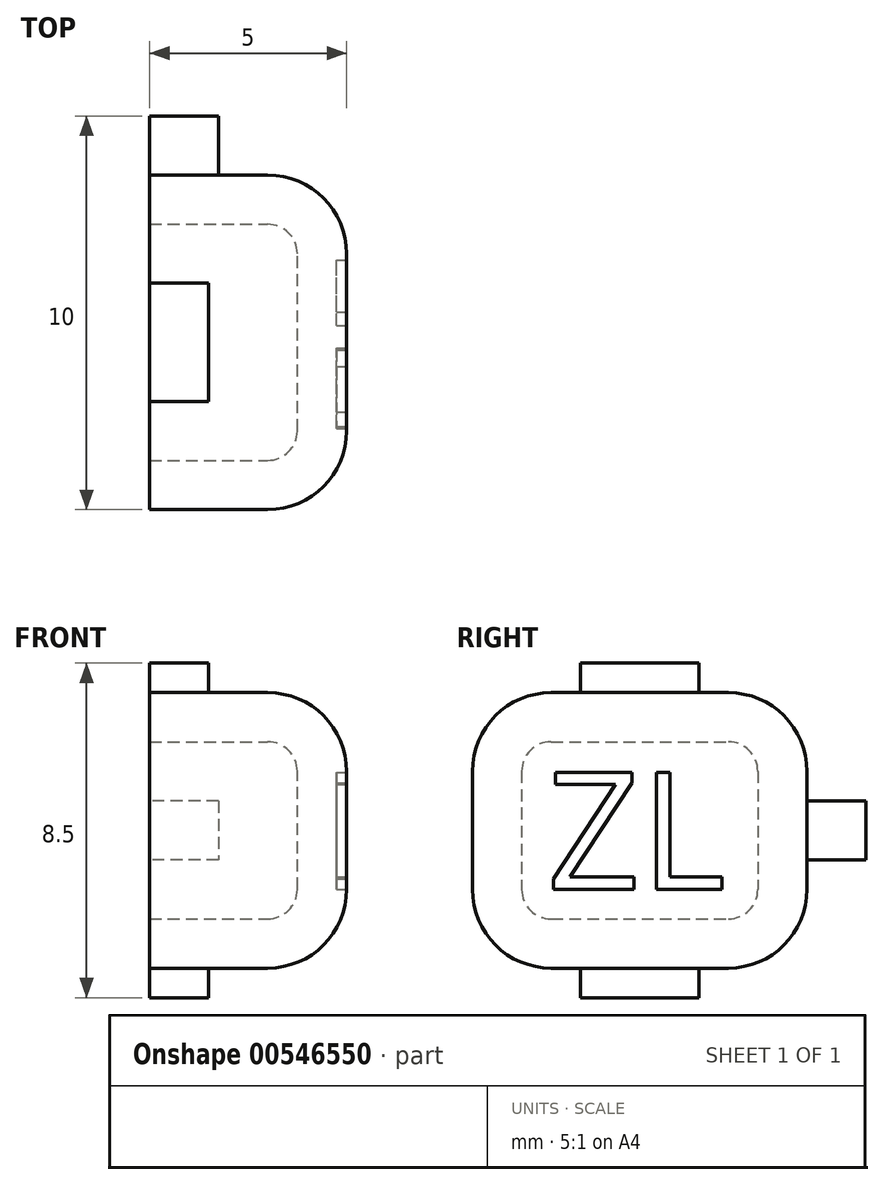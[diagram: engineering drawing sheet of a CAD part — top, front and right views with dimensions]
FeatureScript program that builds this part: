
annotation { "Feature Type Name" : "Feature", "Feature Type Description" : "" }
export const myFeature = defineFeature(function(context is Context, id is Id, definition is map)
    precondition{}
    {
        {
            var Q0;
            Q0=qCreatedBy(makeId("Right.planeOp"),FACE);
            var sketch = newSketch(context, id + "F0", { "sketchPlane" : qUnion([Q0])});
            skLineSegment(sketch, "E0.bottom", {"start": v(-4.25, 3.5) * mm, "end": v(4.25, 3.5) * mm});
            skLineSegment(sketch, "E0.top", {"start": v(-4.25, -3.5) * mm, "end": v(4.25, -3.5) * mm});
            skLineSegment(sketch, "E0.left", {"start": v(-4.25, 3.5) * mm, "end": v(-4.25, -3.5) * mm});
            skLineSegment(sketch, "E0.right", {"start": v(4.25, 3.5) * mm, "end": v(4.25, -3.5) * mm});
            skPoint(sketch, "E0.middle", {"position": v(0, 0) * mm});
            skSolve(sketch);
        }
        {
            var Q0;
            Q0=makeQuery(id+"F0.imprint","IMPRINT",FACE,{"disambiguationData":[TD([[makeQuery(id+"F0.imprint","IMPRINT",EDGE,{"derivedFrom":sQuery(id+"F0.wireOp",EDGE,"E0.bottom")}),-1.0]])]});
            extrude(context, id + "F1", {"entities" : qUnion([Q0]), "endBound" : BoundingType.SYMMETRIC, "depth" : 5 * mm, "offsetDistance" : 25 * mm});
        }
        {
            var Q0;
            Q0=makeQuery(id+"F1.opExtrude","CAP_FACE",FACE,{"disambiguationData":[OSD([sQuery(id+"F0.wireOp",EDGE,"E0.bottom"),sQuery(id+"F0.wireOp",EDGE,"E0.top"),sQuery(id+"F0.wireOp",EDGE,"E0.left"),sQuery(id+"F0.wireOp",EDGE,"E0.right")])],"isStart":false});
            var Q1;
            Q1=makeQuery(id+"F1.opExtrude","SWEPT_EDGE",EDGE,{"disambiguationData":[OSD([sQuery(id+"F0.wireOp",EDGE,"E0.bottom"),sQuery(id+"F0.wireOp",EDGE,"E0.left")])]});
            var Q2;
            Q2=makeQuery(id+"F1.opExtrude","SWEPT_EDGE",EDGE,{"disambiguationData":[OSD([sQuery(id+"F0.wireOp",EDGE,"E0.bottom"),sQuery(id+"F0.wireOp",EDGE,"E0.right")])]});
            var Q3;
            Q3=makeQuery(id+"F1.opExtrude","SWEPT_EDGE",EDGE,{"disambiguationData":[OSD([sQuery(id+"F0.wireOp",EDGE,"E0.top"),sQuery(id+"F0.wireOp",EDGE,"E0.right")])]});
            var Q4;
            Q4=makeQuery(id+"F1.opExtrude","SWEPT_EDGE",EDGE,{"disambiguationData":[OSD([sQuery(id+"F0.wireOp",EDGE,"E0.top"),sQuery(id+"F0.wireOp",EDGE,"E0.left")])]});
            fillet(context, id + "F2", {"entities" : qUnion([Q0, Q1, Q2, Q3, Q4]), "radius" : 2 * mm, "tangentPropagation" : true, "allowEdgeOverflow" : false});
        }
        {
            var Q0;
            Q0=makeQuery(id+"F1.opExtrude","CAP_FACE",FACE,{"disambiguationData":[OSD([sQuery(id+"F0.wireOp",EDGE,"E0.bottom"),sQuery(id+"F0.wireOp",EDGE,"E0.top"),sQuery(id+"F0.wireOp",EDGE,"E0.left"),sQuery(id+"F0.wireOp",EDGE,"E0.right")])],"isStart":true});
            shell(context, id + "F3", {"entities" : qUnion([Q0]), "thickness" : 1.25 * mm});
        }
        {
            var Q0;
            Q0=makeQuery(id+"F1.opExtrude","CAP_FACE",FACE,{"disambiguationData":[OSD([sQuery(id+"F0.wireOp",EDGE,"E0.bottom"),sQuery(id+"F0.wireOp",EDGE,"E0.top"),sQuery(id+"F0.wireOp",EDGE,"E0.left"),sQuery(id+"F0.wireOp",EDGE,"E0.right")])],"isStart":false});
            var sketch = newSketch(context, id + "F4", { "sketchPlane" : qUnion([Q0])});
            skText(sketch, "E1", { "text": "ZL", "fontName": "OpenSans-Regular.ttf"});
            const initialGuessF4  = {"E1": [-0.00236, -0.0015, 1, 0, 0.003]};
            skSetInitialGuess(sketch, initialGuessF4);
            skSolve(sketch);
        }
        {
            var Q0;
            Q0=qSketchRegion(id+"F4",true);
            extrude(context, id + "F5", {"entities" : qUnion([Q0]), "operationType" : NewBodyOperationType.REMOVE, "oppositeDirection" : true, "depth" : .25 * mm, "offsetDistance" : 25 * mm});
        }
        {
            var Q0;
            Q0=makeQuery(id+"F1.opExtrude","CAP_FACE",FACE,{"disambiguationData":[OSD([sQuery(id+"F0.wireOp",EDGE,"E0.bottom"),sQuery(id+"F0.wireOp",EDGE,"E0.top"),sQuery(id+"F0.wireOp",EDGE,"E0.left"),sQuery(id+"F0.wireOp",EDGE,"E0.right")])],"isStart":true});
            var sketch = newSketch(context, id + "F6", { "sketchPlane" : qUnion([Q0])});
            skLineSegment(sketch, "E2.bottom", {"start": v(1.5, 3.5) * mm, "end": v(-1.5, 3.5) * mm});
            skLineSegment(sketch, "E2.top", {"start": v(1.5, 4.25) * mm, "end": v(-1.5, 4.25) * mm});
            skLineSegment(sketch, "E2.left", {"start": v(1.5, 3.5) * mm, "end": v(1.5, 4.25) * mm});
            skLineSegment(sketch, "E2.right", {"start": v(-1.5, 3.5) * mm, "end": v(-1.5, 4.25) * mm});
            skPoint(sketch, "E2.middle", {"position": v(0, 3.87) * mm});
            skLineSegment(sketch, "E3.MirrorCS", {"start": v(1.5, -3.5) * mm, "end": v(1.5, -4.25) * mm});
            skLineSegment(sketch, "E4.MirrorCS", {"start": v(-1.5, -3.5) * mm, "end": v(-1.5, -4.25) * mm});
            skLineSegment(sketch, "E5.MirrorCS", {"start": v(1.5, -4.25) * mm, "end": v(-1.5, -4.25) * mm});
            skLineSegment(sketch, "E6.MirrorCS", {"start": v(1.5, -3.5) * mm, "end": v(-1.5, -3.5) * mm});
            skPoint(sketch, "E7.MirrorP", {"position": v(0, -3.87) * mm});
            skSolve(sketch);
        }
        {
            var Q0;
            Q0=qSketchRegion(id+"F6",true);
            extrude(context, id + "F7", {"entities" : qUnion([Q0]), "operationType" : NewBodyOperationType.ADD, "oppositeDirection" : true, "depth" : 1.5 * mm, "offsetDistance" : 25 * mm});
        }
        {
            var Q0;
            Q0=makeQuery(id+"F1.opExtrude","SWEPT_FACE",FACE,{"disambiguationData":[OSD([sQuery(id+"F0.wireOp",EDGE,"E0.right")])]});
            var sketch = newSketch(context, id + "F8", { "sketchPlane" : qUnion([Q0])});
            skLineSegment(sketch, "E8.bottom", {"start": v(0.75, 0.75) * mm, "end": v(2.5, 0.75) * mm});
            skLineSegment(sketch, "E8.top", {"start": v(0.75, -0.75) * mm, "end": v(2.5, -0.75) * mm});
            skLineSegment(sketch, "E8.left", {"start": v(0.75, 0.75) * mm, "end": v(0.75, -0.75) * mm});
            skLineSegment(sketch, "E8.right", {"start": v(2.5, 0.75) * mm, "end": v(2.5, -0.75) * mm});
            skPoint(sketch, "E8.middle", {"position": v(1.63, 0) * mm});
            skSolve(sketch);
        }
        {
            var Q0;
            Q0=qSketchRegion(id+"F8",true);
            extrude(context, id + "F9", {"entities" : qUnion([Q0]), "operationType" : NewBodyOperationType.ADD, "depth" : 1.5 * mm, "offsetDistance" : 25 * mm});
        }
    });
